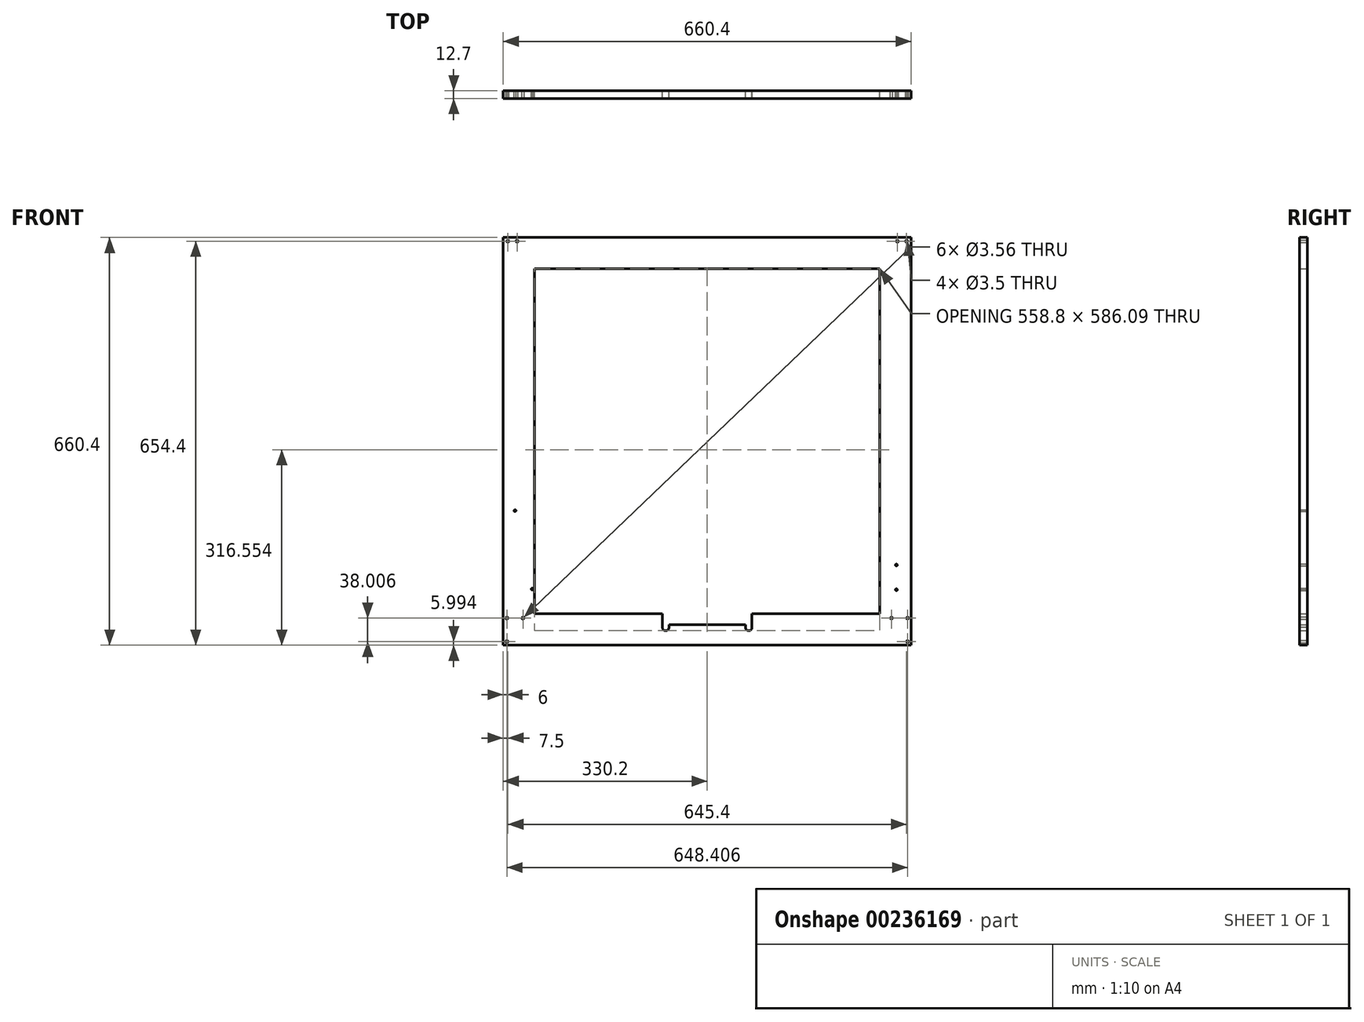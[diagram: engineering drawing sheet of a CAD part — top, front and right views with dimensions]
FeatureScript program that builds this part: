
annotation { "Feature Type Name" : "Feature", "Feature Type Description" : "" }
export const myFeature = defineFeature(function(context is Context, id is Id, definition is map)
    precondition{}
    {
        {
            var Q0;
            Q0=qCreatedBy(makeId("Front.planeOp"),FACE);
            var sketch = newSketch(context, id + "F0", { "sketchPlane" : qUnion([Q0])});
            skLineSegment(sketch, "E0.bottom", {"start": v(-330.2, 330.2) * mm, "end": v(330.2, 330.2) * mm});
            skLineSegment(sketch, "E0.top", {"start": v(-330.2, -330.2) * mm, "end": v(330.2, -330.2) * mm});
            skLineSegment(sketch, "E0.left", {"start": v(-330.2, 330.2) * mm, "end": v(-330.2, -330.2) * mm});
            skLineSegment(sketch, "E0.right", {"start": v(330.2, 330.2) * mm, "end": v(330.2, -330.2) * mm});
            skLineSegment(sketch, "E1.bottom", {"start": v(-279.4, 279.4) * mm, "end": v(279.4, 279.4) * mm});
            skLineSegment(sketch, "E1.top", {"start": v(-279.4, -279.4) * mm, "end": v(-72.48, -279.4) * mm});
            skLineSegment(sketch, "E1.left", {"start": v(-279.4, 279.4) * mm, "end": v(-279.4, -279.4) * mm});
            skLineSegment(sketch, "E1.right", {"start": v(279.4, 279.4) * mm, "end": v(279.4, -279.4) * mm});
            skCircle(sketch, "E2", {"center": v(-324.2, -324.2) * mm, "radius": 1.78 * mm});
            skCircle(sketch, "E3", {"center": v(-324.2, -286.2) * mm, "radius": 1.78 * mm});
            skCircle(sketch, "E4", {"center": v(-298.2, -286.2) * mm, "radius": 1.78 * mm});
            skLineSegment(sketch, "E5", {"start": v(-318.21, -330.2) * mm, "end": v(-318.21, -305.2) * mm});
            skLineSegment(sketch, "E6", {"start": v(-318.21, -305.2) * mm, "end": v(-298.22, -305.2) * mm});
            skLineSegment(sketch, "E7", {"start": v(-298.22, -305.2) * mm, "end": v(-298.22, -330.2) * mm});
            skLineSegment(sketch, "E8", {"start": v(298.22, -330.2) * mm, "end": v(298.22, -305.2) * mm});
            skLineSegment(sketch, "E9", {"start": v(298.22, -305.2) * mm, "end": v(318.21, -305.2) * mm});
            skLineSegment(sketch, "E10", {"start": v(318.21, -305.2) * mm, "end": v(318.21, -330.2) * mm});
            skCircle(sketch, "E11", {"center": v(324.2, -324.2) * mm, "radius": 1.78 * mm});
            skCircle(sketch, "E12", {"center": v(298.2, -286.2) * mm, "radius": 1.78 * mm});
            skCircle(sketch, "E13", {"center": v(324.2, -286.2) * mm, "radius": 1.78 * mm});
            skCircle(sketch, "E14", {"center": v(-322.7, 324.2) * mm, "radius": 1.75 * mm});
            skCircle(sketch, "E15", {"center": v(-307.7, 324.2) * mm, "radius": 1.75 * mm});
            skCircle(sketch, "E16", {"center": v(322.7, 324.2) * mm, "radius": 1.75 * mm});
            skCircle(sketch, "E17", {"center": v(307.7, 324.2) * mm, "radius": 1.75 * mm});
            skCircle(sketch, "E18", {"center": v(-283.4, -239.2) * mm, "radius": 1.5 * mm});
            skCircle(sketch, "E19", {"center": v(-311.2, -112.2) * mm, "radius": 1.5 * mm});
            skCircle(sketch, "E20", {"center": v(306.2, -200.2) * mm, "radius": 1.5 * mm});
            skCircle(sketch, "E21", {"center": v(306.2, -240.2) * mm, "radius": 1.5 * mm});
            skArc(sketch, "E22", {"start": v(-72.48, -301.45) * mm, "mid": v(-66.8, -306.67) * mm, "end": v(-62.06, -300.57) * mm});
            skArc(sketch, "E23", {"start": v(62.09, -300.57) * mm, "mid": v(67.32, -306.7) * mm, "end": v(72.4, -300.45) * mm});
            skLineSegment(sketch, "E24", {"start": v(-72.48, -301.45) * mm, "end": v(-72.48, -279.4) * mm});
            skLineSegment(sketch, "E25", {"start": v(-62.06, -302.33) * mm, "end": v(-62.06, -300.57) * mm});
            skLineSegment(sketch, "E26", {"start": v(72.4, -300.45) * mm, "end": v(72.4, -279.4) * mm});
            skLineSegment(sketch, "E27", {"start": v(-62.06, -297.18) * mm, "end": v(62.09, -297.18) * mm});
            skLineSegment(sketch, "E28.trimOffspring", {"start": v(72.4, -279.4) * mm, "end": v(279.4, -279.4) * mm});
            skLineSegment(sketch, "E29", {"start": v(62.09, -302.32) * mm, "end": v(62.09, -297.18) * mm});
            skLineSegment(sketch, "E30", {"start": v(-62.06, -297.18) * mm, "end": v(-62.06, -302.33) * mm});
            skSolve(sketch);
        }
        {
            var Q0;
            Q0 = qSketchRegion(id + "F0", true);
            extrude(context, id + "F1", {"entities" : qUnion([Q0]), "depth" : 12.7 * mm});
        }
    });
